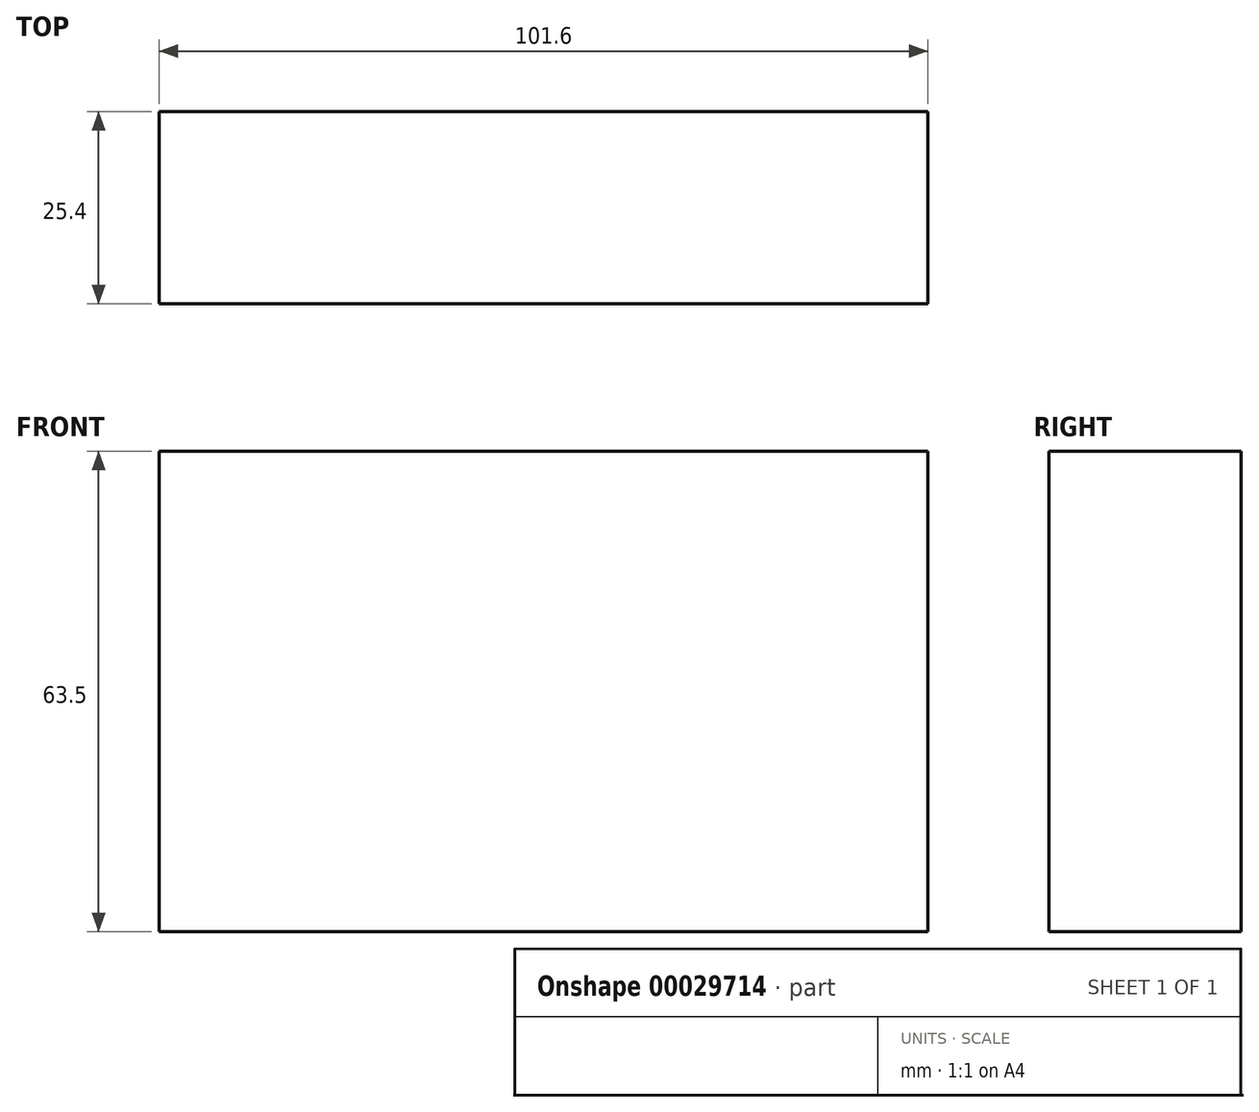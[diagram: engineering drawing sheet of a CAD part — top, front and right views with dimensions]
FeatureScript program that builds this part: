
annotation { "Feature Type Name" : "Feature", "Feature Type Description" : "" }
export const myFeature = defineFeature(function(context is Context, id is Id, definition is map)
    precondition{}
    {
        {
            var Q0;
            Q0=qCreatedBy(makeId("Front.planeOp"),FACE);
            var sketch = newSketch(context, id + "F0", { "sketchPlane" : qUnion([Q0])});
            skLineSegment(sketch, "E0.bottom", {"start": v(-50.8, 31.75) * mm, "end": v(50.8, 31.75) * mm});
            skLineSegment(sketch, "E0.top", {"start": v(-50.8, -31.75) * mm, "end": v(50.8, -31.75) * mm});
            skLineSegment(sketch, "E0.left", {"start": v(-50.8, 31.75) * mm, "end": v(-50.8, -31.75) * mm});
            skLineSegment(sketch, "E0.right", {"start": v(50.8, 31.75) * mm, "end": v(50.8, -31.75) * mm});
            skLineSegment(sketch, "E1", {"start": v(-50.8, 31.75) * mm, "end": v(50.8, -31.75) * mm, "construction": true});
            skSolve(sketch);
        }
        {
            var Q0;
            Q0 = qSketchRegion(id + "F0", true);
            extrude(context, id + "F1", {"entities" : qUnion([Q0]), "depth" : 25.4 * mm});
        }
    });
